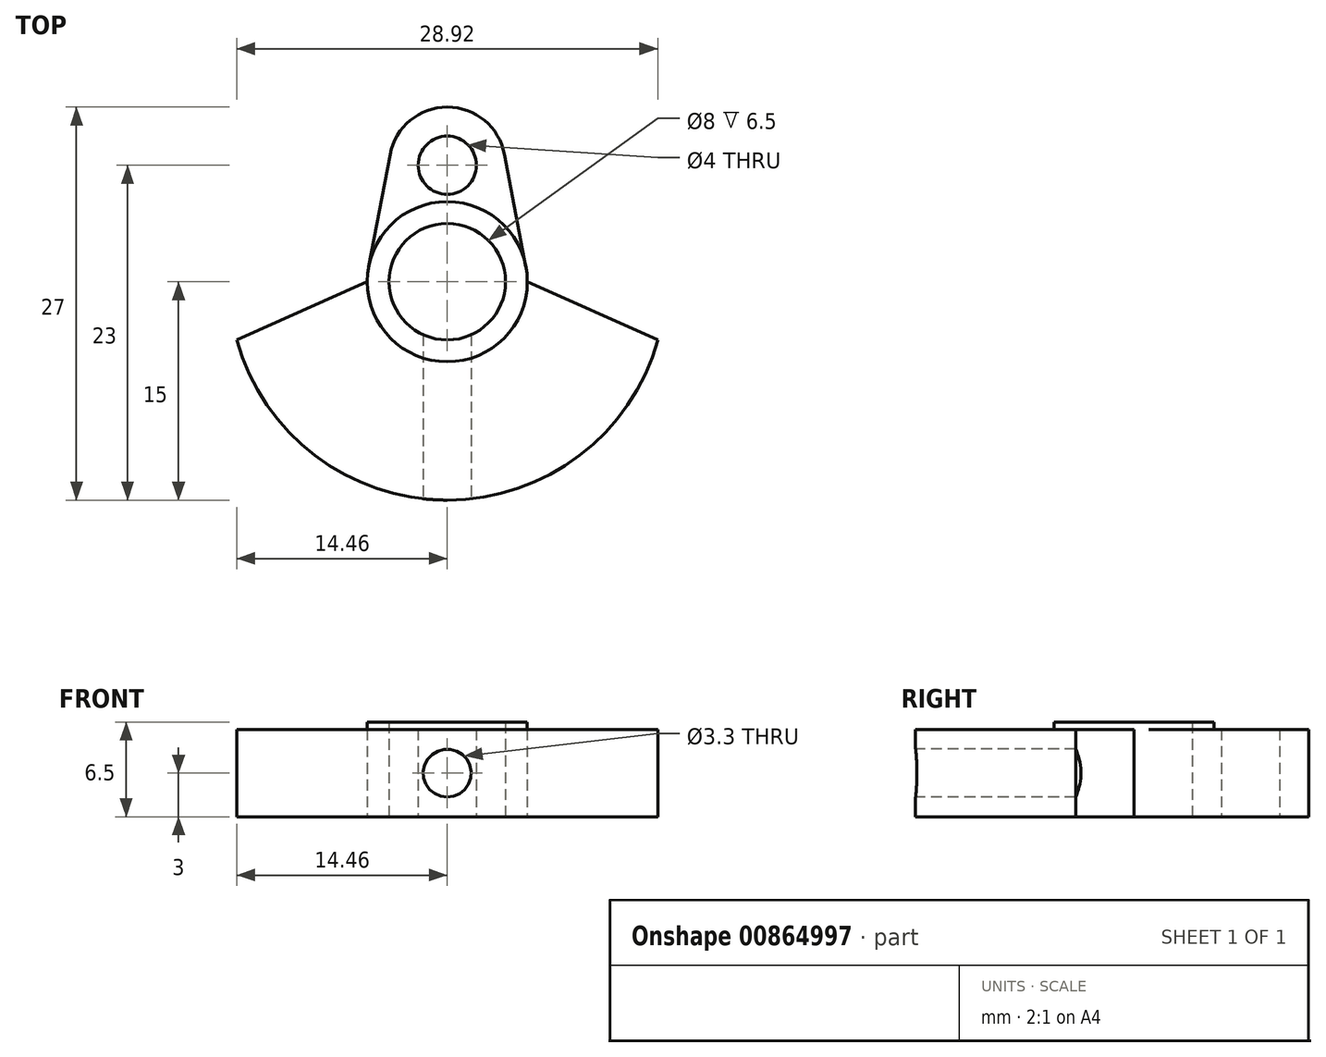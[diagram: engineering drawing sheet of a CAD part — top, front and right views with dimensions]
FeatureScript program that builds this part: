
annotation { "Feature Type Name" : "Feature", "Feature Type Description" : "" }
export const myFeature = defineFeature(function(context is Context, id is Id, definition is map)
    precondition{}
    {
        {
            var Q0;
            Q0=qCreatedBy(makeId("Top.planeOp"),FACE);
            var sketch = newSketch(context, id + "F0", { "sketchPlane" : qUnion([Q0])});
            skCircle(sketch, "E0", {"center": v(0, 0) * mm, "radius": 5.5 * mm});
            skCircle(sketch, "E1", {"center": v(0, 0) * mm, "radius": 4 * mm});
            skCircle(sketch, "E2", {"center": v(0, 8) * mm, "radius": 2 * mm});
            skArc(sketch, "E3", {"start": v(-14.46, -4) * mm, "mid": v(0, -15) * mm, "end": v(14.46, -4) * mm});
            skLineSegment(sketch, "E4", {"start": v(-14.46, -4) * mm, "end": v(-5.5, 0) * mm});
            skLineSegment(sketch, "E5", {"start": v(14.46, -4) * mm, "end": v(5.5, 0) * mm});
            skLineSegment(sketch, "E6", {"start": v(-3.93, 8.75) * mm, "end": v(-5.4, 1.03) * mm});
            skLineSegment(sketch, "E7", {"start": v(3.93, 8.75) * mm, "end": v(5.4, 1.03) * mm});
            skArc(sketch, "E8.trimOffspring", {"start": v(3.93, 8.75) * mm, "mid": v(0, 12) * mm, "end": v(-3.93, 8.75) * mm});
            skSolve(sketch);
        }
        {
            var Q0;
            Q0=qCreatedBy(makeId("Front.planeOp"),FACE);
            cPlane(context, id + "F1", {"entities" : qUnion([Q0]), "cplaneType" : CPlaneType.OFFSET, "offset" : 15 * mm, "width" : 150 * mm, "height" : 150 * mm});
        }
        {
            var Q0;
            Q0=makeQuery(id+"F0.imprint","IMPRINT",FACE,{"disambiguationData":[TD([[makeQuery(id+"F0.imprint","IMPRINT",EDGE,{"derivedFrom":sQuery(id+"F0.wireOp",EDGE,"E1")}),-1.0]])]});
            extrude(context, id + "F2", {"entities" : qUnion([Q0]), "depth" : 6.5 * mm, "offsetDistance" : 25 * mm});
        }
        {
            var Q0;
            Q0=makeQuery(id+"F0.imprint","IMPRINT",FACE,{"disambiguationData":[TD([[makeQuery(id+"F0.imprint","IMPRINT",EDGE,{"derivedFrom":sQuery(id+"F0.wireOp",EDGE,"E2")}),-1.0]])]});
            var Q1;
            Q1=makeQuery(id+"F0.imprint","IMPRINT",FACE,{"disambiguationData":[TD([[makeQuery(id+"F0.imprint","IMPRINT",EDGE,{"derivedFrom":sQuery(id+"F0.wireOp",EDGE,"E3")}),1.0]])]});
            extrude(context, id + "F3", {"entities" : qUnion([Q0, Q1]), "operationType" : NewBodyOperationType.ADD, "depth" : 6 * mm, "offsetDistance" : 25 * mm});
        }
        {
            var Q0;
            Q0=qCreatedBy(id+"F1.planeOp",FACE);
            var sketch = newSketch(context, id + "F4", { "sketchPlane" : qUnion([Q0])});
            skPoint(sketch, "E9", {"position": v(0, 3) * mm});
            skSolve(sketch);
        }
        {
            var Q0;
            Q0=sQuery(id+"F4.wireOp",VERTEX,"E9");
            var Q1;
            Q1=makeQuery(id+"F2.opExtrude","SWEPT_BODY",BODY,{"disambiguationData":[OSD([sQuery(id+"F0.wireOp",EDGE,"E0"),sQuery(id+"F0.wireOp",EDGE,"E1")])]});
            hole(context, id + "F5", {"style" : HoleStyle.SIMPLE, "endStyle" : HoleEndStyle.BLIND, "standardTappedOrClearance" : lookupTablePath({ "standard" : "ISO", "engagement" : "75%", "pitch" : "0.7 mm", "size" : "M4", "type" : "Tapped" }), "standardBlindInLast" : lookupTablePath({ "standard" : "ISO", "engagement" : "75%", "pitch" : "0.7 mm", "size" : "M4", "type" : "Tapped" }), "holeDiameter" : 3.3 * mm, "majorDiameter" : 4 * mm, "showTappedDepth" : true, "holeDepth" : 15 * mm, "isTappedThrough" : true, "tappedDepth" : 15 * mm, "tapClearance" : 0, "startFromSketch" : true, "locations" : qUnion([Q0]), "scope" : qUnion([Q1])});
        }
    });
